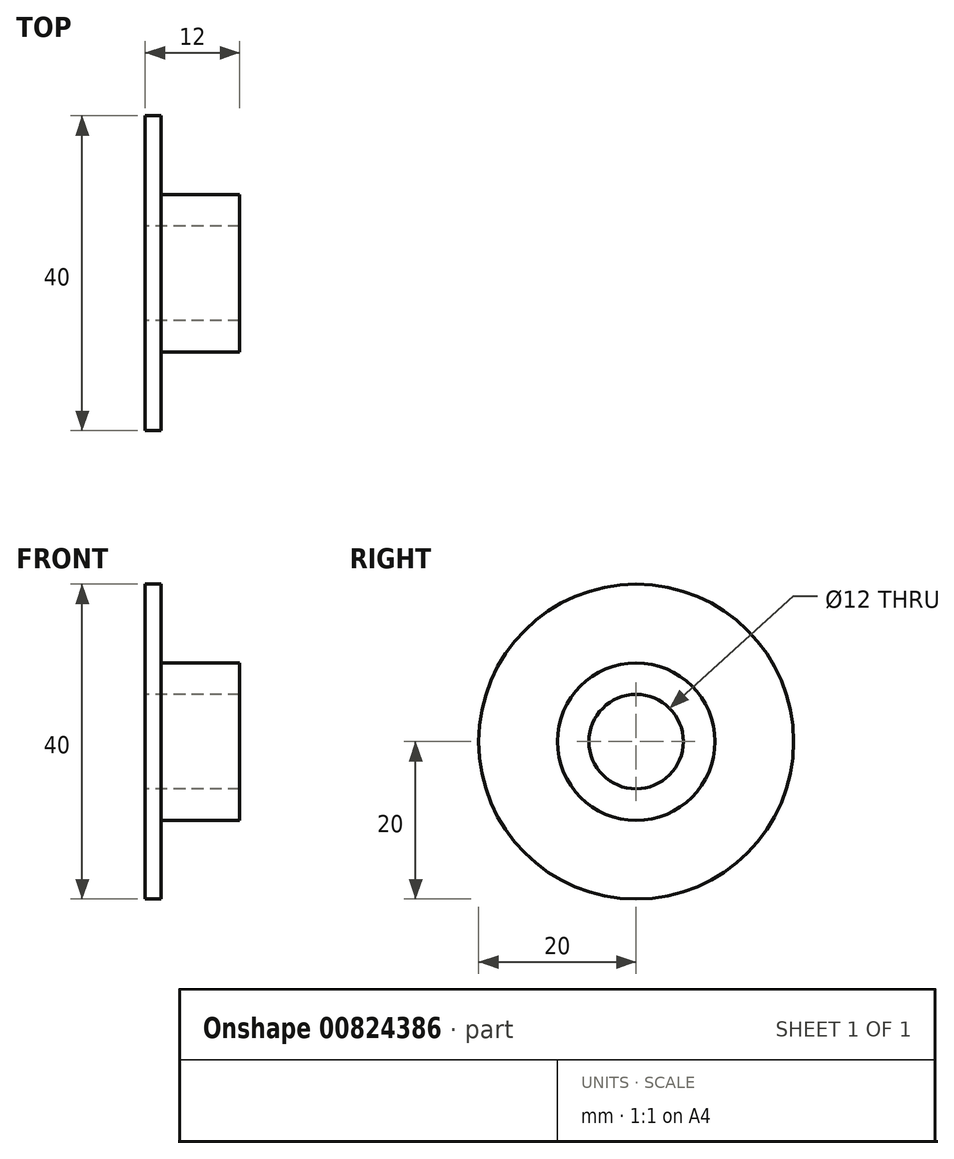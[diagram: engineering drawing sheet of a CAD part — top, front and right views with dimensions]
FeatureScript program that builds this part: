
annotation { "Feature Type Name" : "Feature", "Feature Type Description" : "" }
export const myFeature = defineFeature(function(context is Context, id is Id, definition is map)
    precondition{}
    {
        {
            var Q0;
            Q0=qCreatedBy(makeId("Front.planeOp"),FACE);
            var sketch = newSketch(context, id + "F0", { "sketchPlane" : qUnion([Q0])});
            skLineSegment(sketch, "E0", {"start": v(0, 6) * mm, "end": v(0, 20) * mm});
            skLineSegment(sketch, "E1", {"start": v(0, 20) * mm, "end": v(2, 20) * mm});
            skLineSegment(sketch, "E2", {"start": v(2, 20) * mm, "end": v(2, 10) * mm});
            skLineSegment(sketch, "E3", {"start": v(2, 10) * mm, "end": v(12, 10) * mm});
            skLineSegment(sketch, "E4", {"start": v(12, 10) * mm, "end": v(12, 6) * mm});
            skLineSegment(sketch, "E5", {"start": v(12, 6) * mm, "end": v(0, 6) * mm});
            skLineSegment(sketch, "E6", {"start": v(0, 0) * mm, "end": v(513.86, 0) * mm, "construction": true});
            skSolve(sketch);
        }
        {
            var Q0;
            Q0=qSketchRegion(id+"F0",true);
            var Q1;
            Q1=qConstructionFilter(qBodyType(qCreatedBy(id+"F0",EDGE),BodyType.WIRE),ConstructionObject.NO);
            var Q2;
            Q2=sQuery(id+"F0.wireOp",EDGE,"E6");
            revolve(context, id + "F1", {"surfaceOperationType" : NewSurfaceOperationType.NEW, "entities" : qUnion([Q0]), "surfaceEntities" : qUnion([Q1]), "axis" : qUnion([Q2]), "revolveType" : RevolveType.FULL});
        }
    });
